FCSTD DOCUMENT  (FreeCAD 0.22R37645 (Git))
Label: ipad stand
License: All rights reserved
LicenseURL: http://en.wikipedia.org/wiki/All_rights_reserved
objects: Sketcher::SketchObject×2
note: 2 computed .brp shape members not serialized (recipe doc carries the construction recipe); baked Part::Feature solids carry a one-line shape summary decoded from their .brp

FEATURE [Sketcher::SketchObject] Sketch003  label="base"
  FullyConstrained = false
  sketch-geometry (32):
    g0: LineSegment StartX=-51.8192 StartY=44.2862 StartZ=0 EndX=-61.8471 EndY=29.9648 EndZ=0
    g1: LineSegment StartX=-61.8471 StartY=29.9648 StartZ=0 EndX=-66.0247 EndY=32.8901 EndZ=0
    g2: LineSegment StartX=-66.0247 StartY=32.8901 StartZ=0 EndX=-62.0097 EndY=38.6241 EndZ=0
    g3: LineSegment StartX=-62.2553 StartY=40.0169 StartZ=0 EndX=-76.1809 EndY=49.7677 EndZ=0
    g4: LineSegment StartX=-76.1809 StartY=49.7677 StartZ=0 EndX=-68.1508 EndY=61.2358 EndZ=0
    g5: ArcOfCircle CenterX=-68.9699 CenterY=61.8094 CenterZ=0 NormalX=0 NormalY=0 NormalZ=1 AngleXU=0 Radius=1 StartAngle=5.67232 EndAngle=7.85398
    g6: GeomPoint X=-68.1508 Y=61.2358 Z=0
    g7: ArcOfCircle CenterX=-62.8288 CenterY=39.1977 CenterZ=0 NormalX=0 NormalY=0 NormalZ=1 AngleXU=0 Radius=1 StartAngle=5.67232 EndAngle=7.24312
    g8: GeomPoint X=-61.4361 Y=39.4433 Z=0
    g9: ArcOfCircle CenterX=-51 CenterY=43.7126 CenterZ=0 NormalX=0 NormalY=0 NormalZ=1 AngleXU=0 Radius=1 StartAngle=1.5708 EndAngle=2.53073
    g10: GeomPoint X=-53.2434 Y=42.2521 Z=0
    g11: ArcOfCircle CenterX=-68.9699 CenterY=40.8094 CenterZ=0 NormalX=0 NormalY=0 NormalZ=1 AngleXU=0 Radius=22 StartAngle=1.5708 EndAngle=5.29105
    g12: ArcOfCircle CenterX=-46 CenterY=5.64715 CenterZ=0 NormalX=0 NormalY=0 NormalZ=1 AngleXU=0 Radius=20 StartAngle=1.5708 EndAngle=2.14946
    g13: GeomPoint X=-66.4357 Y=23.4116 Z=0
    g14: LineSegment StartX=-51 StartY=44.7126 StartZ=0 EndX=-50 EndY=44.7126 EndZ=0
    g15: LineSegment StartX=51.9397 StartY=44.0546 StartZ=0 EndX=56.0439 EndY=32.7783 EndZ=0
    g16: LineSegment StartX=56.0439 StartY=32.7783 StartZ=0 EndX=60.8364 EndY=34.5226 EndZ=0
    g17: LineSegment StartX=60.8364 StartY=34.5226 StartZ=0 EndX=58.4422 EndY=41.1004 EndZ=0
    g18: LineSegment StartX=59.0399 StartY=42.3822 StartZ=0 EndX=75.0147 EndY=48.1965 EndZ=0
    g19: LineSegment StartX=75.0147 StartY=48.1965 StartZ=0 EndX=70.2264 EndY=61.3522 EndZ=0
    g20: ArcOfCircle CenterX=71.1661 CenterY=61.6942 CenterZ=0 NormalX=0 NormalY=0 NormalZ=1 AngleXU=0 Radius=1 StartAngle=1.46603 EndAngle=3.49066
    g21: GeomPoint X=70.2264 Y=61.3522 Z=0
    g22: ArcOfCircle CenterX=59.3819 CenterY=41.4425 CenterZ=0 NormalX=0 NormalY=0 NormalZ=1 AngleXU=0 Radius=1 StartAngle=1.91986 EndAngle=3.49066
    g23: GeomPoint X=58.1002 Y=42.0401 Z=0
    g24: ArcOfCircle CenterX=51 CenterY=43.7126 CenterZ=0 NormalX=0 NormalY=0 NormalZ=1 AngleXU=0 Radius=1 StartAngle=0.349066 EndAngle=1.5708
    g25: GeomPoint X=50.9136 Y=46.8737 Z=0
    g26: ArcOfCircle CenterX=68.9699 CenterY=40.8094 CenterZ=0 NormalX=0 NormalY=0 NormalZ=1 AngleXU=0 Radius=22 StartAngle=4.13373 EndAngle=7.74921
    g27: ArcOfCircle CenterX=46 CenterY=5.64715 CenterZ=0 NormalX=0 NormalY=0 NormalZ=1 AngleXU=0 Radius=20 StartAngle=0.992135 EndAngle=1.5708
    g28: GeomPoint X=58.7801 Y=25.2608 Z=0
    g29: LineSegment StartX=51 StartY=44.7126 StartZ=0 EndX=50 EndY=44.7126 EndZ=0
    g30: LineSegment StartX=46 StartY=25.6471 StartZ=0 EndX=-46 EndY=25.6471 EndZ=0
    g31: LineSegment StartX=50 StartY=44.7126 StartZ=0 EndX=-50 EndY=44.7126 EndZ=0
  constraints (80):
    c: Coincident(g0,g1)
    c: Coincident(g1,g2)
    c: Coincident(g3,g4)
    c: Perpendicular(g1,g0)
    c: Parallel(g0,g2)
    c: Parallel(g4,g2)
    c: Perpendicular(g2,g3)
    c: Distance(g1) = 5.1
    c: Distance(g3,g8) = 18
    c: Distance(g2,g8) = 8
    c: Distance(g0,g10) = 15
    c: Distance(g4,g6) = 14
    c: PointOnObject(g6,g4)
    c: Tangent(g4,g5) = -1.5708
    c: PointOnObject(g8,g3)
    c: PointOnObject(g8,g2)
    c: Tangent(g3,g7) = -1.5708
    c: Tangent(g2,g7) = -1.5708
    c: PointOnObject(g10,g0)
    c: Tangent(g0,g9) = -1.5708
    c: Equal(g5,g7)
    c: Equal(g5,g9)
    c: Radius(g5) = 1
    c: Tangent(g11,g5) = -1.5708
    c: Vertical(g5,g11)
    c: Distance(g4) = 14
    c: Radius(g11) = 22
    c: Tangent(g11,g12) = 1.5708
    c: Radius(g12) = 20
    c: PointOnObject(g13,g0)
    c: Distance(g13,g0) = 8
    c: Vertical(g12,g12)
    c: DistanceX(g14,g14) = 1
    c: Tangent(g14,g9) = 1.5708
    c: Horizontal(g14)
    c: DistanceX(g14,g12) = 4
    c: Coincident(g15,g16)
    c: Coincident(g16,g17)
    c: Coincident(g18,g19)
    c: Perpendicular(g16,g15)
    c: Parallel(g15,g17)
    c: Parallel(g19,g17)
    c: Perpendicular(g17,g18)
    c: Distance(g16) = 5.1
    c: Distance(g18,g23) = 18
    c: Distance(g17,g23) = 8
    c: Distance(g15,g25) = 15
    c: Distance(g19,g21) = 14
    c: PointOnObject(g21,g19)
    c: Tangent(g19,g20) = 1.5708
    c: PointOnObject(g23,g18)
    c: PointOnObject(g23,g17)
    c: Tangent(g18,g22) = 1.5708
    c: Tangent(g17,g22) = 1.5708
    c: PointOnObject(g25,g15)
    c: Tangent(g15,g24) = 1.5708
    c: Equal(g20,g22)
    c: Equal(g20,g24)
    c: Radius(g20) = 1
    c: Tangent(g26,g20) = -1.5708
    c: Distance(g19) = 14
    c: Radius(g26) = 22
    c: Tangent(g26,g27) = 1.5708
    c: Radius(g27) = 20
    c: PointOnObject(g28,g15)
    c: Distance(g28,g15) = 8
    c: Tangent(g29,g24) = -1.5708
    c: Horizontal(g29)
    c: Distance(g15) = 12
    c: Angle(g-1,g2) = 0.959931
    c: Angle(g15,g-1) = 1.22173
    c: Coincident(g30,g27)
    c: Coincident(g30,g12)
    c: Coincident(g31,g29)
    c: Coincident(g31,g14)
    c: Symmetric(g12,g27,g-2)
    c: Symmetric(g11,g26,g-2)
    c: Symmetric(g14,g29,g-2)
    c: Equal(g29,g14)
    c: DistanceX(g31,g31) = 100
FEATURE [Sketcher::SketchObject] Sketch  label="back"
  FullyConstrained = true
  sketch-geometry (20):
    g0: LineSegment StartX=-100 StartY=70 StartZ=0 EndX=-100 EndY=-70 EndZ=0
    g1: LineSegment StartX=-90 StartY=-80 StartZ=0 EndX=-80 EndY=-80 EndZ=0
    g2: LineSegment StartX=100 StartY=-70 StartZ=0 EndX=100 EndY=70 EndZ=0
    g3: LineSegment StartX=90 StartY=80 StartZ=0 EndX=-90 EndY=80 EndZ=0
    g4: ArcOfCircle CenterX=-90 CenterY=70 CenterZ=0 NormalX=0 NormalY=0 NormalZ=1 AngleXU=0 Radius=10 StartAngle=1.5708 EndAngle=3.14159
    g5: GeomPoint X=-100 Y=80 Z=0
    g6: ArcOfCircle CenterX=90 CenterY=70 CenterZ=0 NormalX=0 NormalY=0 NormalZ=1 AngleXU=0 Radius=10 StartAngle=6e-16 EndAngle=1.5708
    g7: GeomPoint X=100 Y=80 Z=0
    g8: ArcOfCircle CenterX=90 CenterY=-70 CenterZ=0 NormalX=0 NormalY=0 NormalZ=1 AngleXU=0 Radius=10 StartAngle=4.71239 EndAngle=6.28319
    g9: GeomPoint X=100 Y=-80 Z=0
    g10: ArcOfCircle CenterX=-90 CenterY=-70 CenterZ=0 NormalX=0 NormalY=0 NormalZ=1 AngleXU=0 Radius=10 StartAngle=3.14159 EndAngle=4.71239
    g11: GeomPoint X=-100 Y=-80 Z=0
    g12: LineSegment StartX=-75 StartY=-80 StartZ=0 EndX=-75 EndY=-72 EndZ=0
    g13: LineSegment StartX=-75 StartY=-72 StartZ=0 EndX=-80 EndY=-72 EndZ=0
    g14: LineSegment StartX=-80 StartY=-72 StartZ=0 EndX=-80 EndY=-80 EndZ=0
    g15: LineSegment StartX=80 StartY=-80 StartZ=0 EndX=80 EndY=-72 EndZ=0
    g16: LineSegment StartX=80 StartY=-72 StartZ=0 EndX=75 EndY=-72 EndZ=0
    g17: LineSegment StartX=75 StartY=-72 StartZ=0 EndX=75 EndY=-80 EndZ=0
    g18: LineSegment StartX=-75 StartY=-80 StartZ=0 EndX=75 EndY=-80 EndZ=0
    g19: LineSegment StartX=80 StartY=-80 StartZ=0 EndX=90 EndY=-80 EndZ=0
  constraints (50):
    c: Vertical(g0)
    c: Vertical(g2)
    c: Horizontal(g1)
    c: Horizontal(g3)
    c: Symmetric(g11,g7,g-1)
    c: DistanceX(g11,g9) = 200
    c: DistanceY(g11,g5) = 160
    c: PointOnObject(g5,g0)
    c: PointOnObject(g5,g3)
    c: Tangent(g0,g4) = -1.5708
    c: Tangent(g3,g4) = -1.5708
    c: PointOnObject(g7,g2)
    c: PointOnObject(g7,g3)
    c: Tangent(g2,g6) = -1.5708
    c: Tangent(g3,g6) = -1.5708
    c: PointOnObject(g9,g1)
    c: PointOnObject(g9,g2)
    c: Tangent(g2,g8) = -1.5708
    c: PointOnObject(g11,g0)
    c: PointOnObject(g11,g1)
    c: Tangent(g0,g10) = -1.5708
    c: Tangent(g1,g10) = -1.5708
    c: Equal(g4,g6)
    c: Radius(g4) = 10
    c: Equal(g8,g6)
    c: Equal(g8,g10)
    c: Coincident(g12,g13)
    c: Coincident(g13,g14)
    c: Horizontal(g13)
    c: Vertical(g12)
    c: Vertical(g14)
    c: Coincident(g15,g16)
    c: Coincident(g16,g17)
    c: Horizontal(g16)
    c: Vertical(g15)
    c: Vertical(g17)
    c: DistanceX(g13,g13) = 5
    c: Equal(g13,g16)
    c: Equal(g12,g17)
    c: Symmetric(g17,g12,g-2)
    c: DistanceX(g12,g17) = 150
    c: Coincident(g12,g18)
    c: Coincident(g17,g18)
    c: Horizontal(g17,g15)
    c: Horizontal(g12,g1)
    c: Coincident(g19,g15)
    c: Horizontal(g19)
    c: Coincident(g1,g14)
    c: Tangent(g19,g8) = -1.5708
    c: DistanceY(g15,g15) = 8
